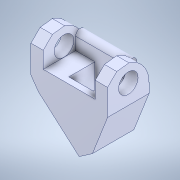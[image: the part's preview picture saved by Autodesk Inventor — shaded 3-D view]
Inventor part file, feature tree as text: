
AUTODESK INVENTOR PART (.ipt)
format: ipt  version: 2022 (Build 260153000, 153)  size: 156,160 bytes
history: mixed  units: mm
features: other x2, extrude x1, fillet x1, sketch x1, imported_body x1
ambient origin geometry x8: Origin, YZ Plane, XZ Plane, XY Plane, X Axis, Y Axis, Z Axis, Center Point
bodies: Body1 (imported_parasolid)
feature tree (6):
  other  "Sólido1"
  extrude  "Extrusión1"  Depth=1.87mm TaperAngle=0.0deg
  fillet  "Empalme2"  Radius=1.87mm
  sketch  "Boceto2"  dims[d0=0.0mm d1=7.0mm d2=0.0mm d4=1.87mm d5=0.0mm d6=0.0mm d7=0.0mm]
  other  "Cut-Extrude3"
  imported_body  NMx_Import_Brep_tag  [imported B-rep: ~29 faces, bbox_mm=[31.41555, 34.739063, 17.0]]
